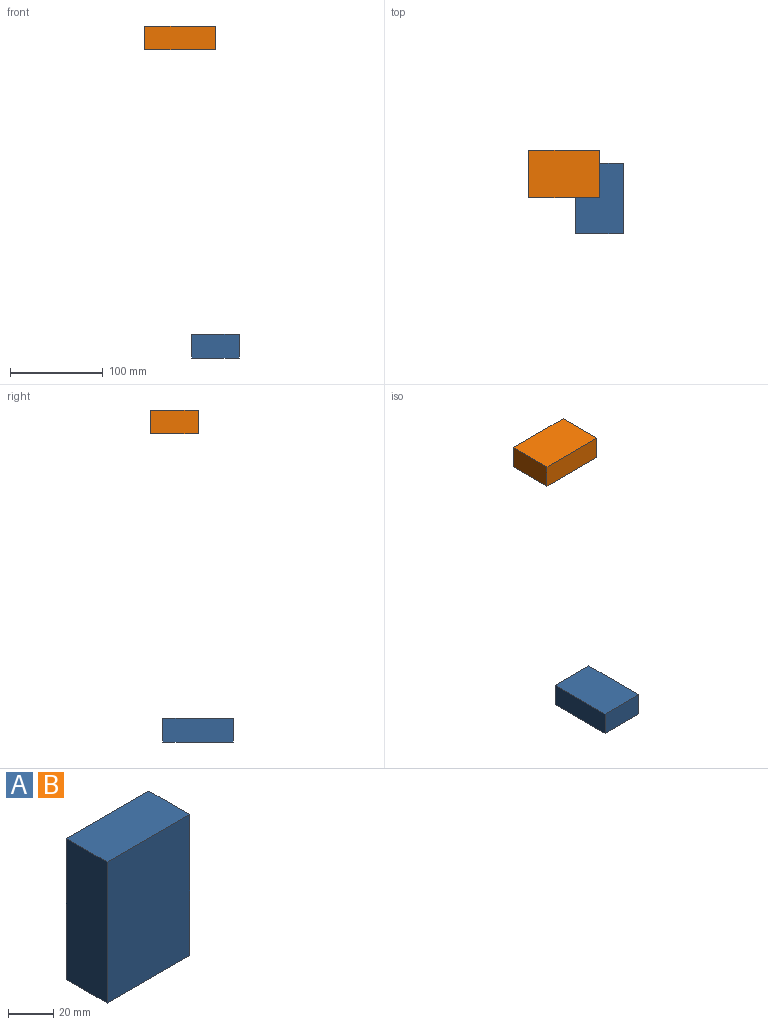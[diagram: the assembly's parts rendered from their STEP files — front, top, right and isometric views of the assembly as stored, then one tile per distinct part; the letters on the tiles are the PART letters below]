
ASSEMBLY  parts=2 mates=1
PART A: 6 faces, bbox 51.4x25.4x76.1 mm
  f0: plane 51.42x25.4mm, normal (0,0,1), area 1306mm2, adj f1,f3,f4,f5
  f1: plane 76.15x25.4mm, normal (-1,0,0), area 1934.1mm2, adj f0,f2,f4,f5
  f2: plane 51.42x25.4mm, normal (0,0,-1), area 1306mm2, adj f1,f3,f4,f5
  f3: plane 76.15x25.4mm, normal (1,0,0), area 1934.1mm2, adj f0,f2,f4,f5
  f4: plane 76.15x51.42mm, normal (0,-1,0), area 3915.4mm2, adj f0,f1,f2,f3
  f5: plane 76.15x51.42mm, normal (0,1,0), area 3915.4mm2, adj f0,f1,f2,f3
PART B: same geometry as A
PLACE A rot(axis=(0,0.71,0.71),180deg) t=(346.35,31.45,-220.04)mm
PLACE B rot(axis=(-0.58,0.58,-0.58),120deg) t=(316.46,48.98,87.3)mm
MATE cylindrical B.f4 <-> A.f5  axis (0,0,1) through (372.06,48.98,112.7)mm
